# Revit family: Seating-Casual-Naughtone-Construct_CnterHght_Stool
name_source: partatom
category: Furniture
revit_build: Autodesk Revit 2015 (Build: 20150704_0715(x64)
units: mm (PartAtom-declared; Revit-internal decimal feet)

## types (1)
- 435mmx435mmx660mm
    Assembly Code = E2020200
    AssetIdentifier = CON-CBS
    AssetType = Movable
    BIMObjectName = Seating-Casual-Naughtone-Construct_CnterHght_Stool
    BarCode = 0.000000
    Category = 40.50.12.85 : Stools
    CodePerformance = FISP; ISO14001 Certified
    Color = Oak
    ComponentDescription = The construct range is a wonderfully useful product range that can be dropped into almost any situation. Construct has a fine balance of materials with a solid oak top and a folded steel base that wears it's construction method on its sleeve.
    Constituents = Solid Oak Top; Folded mild steel
    Cost = 0 $
    Description = Construct Counter Height Stool
    DurationUnit = Years
    ExpectedLife = 15-20
    Finish = Matt Lacquer
    Grade = 3
    Keynote = 40.50.12.85
    Manufacturer = Naughtone
    ManufacturerDetailsUK = 201 Pannal Business Park, Station Road, Harrogate, HG3 1JL
    Material = Wood; Steel
    Model = CON-CBS
    ModelNumber = CON-CBS
    ModelReference = Construct Counter Height Stool
    NBSReference = 40.50.12.85
    Name = Seating-Casual-Naughtone-Construct_CnterHght_Stool
    NominalHeight = 660 mm
    NominalLength = 435 mm
    NominalWidth = 435 mm
    Product URL = http://www.naughtone.com
    ProductInformation = http://www.naughtone.com
    ReplacementCost = 0.00
    SerialNumber = 0.000000
    Shape = Circular
    Size = 435mmx435mmx660mm
    SustainabilityPerformance = 84.4% Recyclable
    TagNumber = 0
    Type Comments = 435x435x660
    TypeName = 435mmx435mmx660mm, Construct Counter Height Stool
    URL = http://www.naughtone.com
    Uniclass2015 = 40.50.12.85
    Version = 1
    WarrantyDescription = 5 Year Warranty
    WarrantyDurationLabor = 5
    WarrantyDurationParts = 5
    WarrantyDurationUnit = Years
    _current revision = 1
    _distributed by = www.bimbox.co.uk

## geometry (parser evidence)
native form markers: Sweep x2
no freeform markers — native parametric forms only
